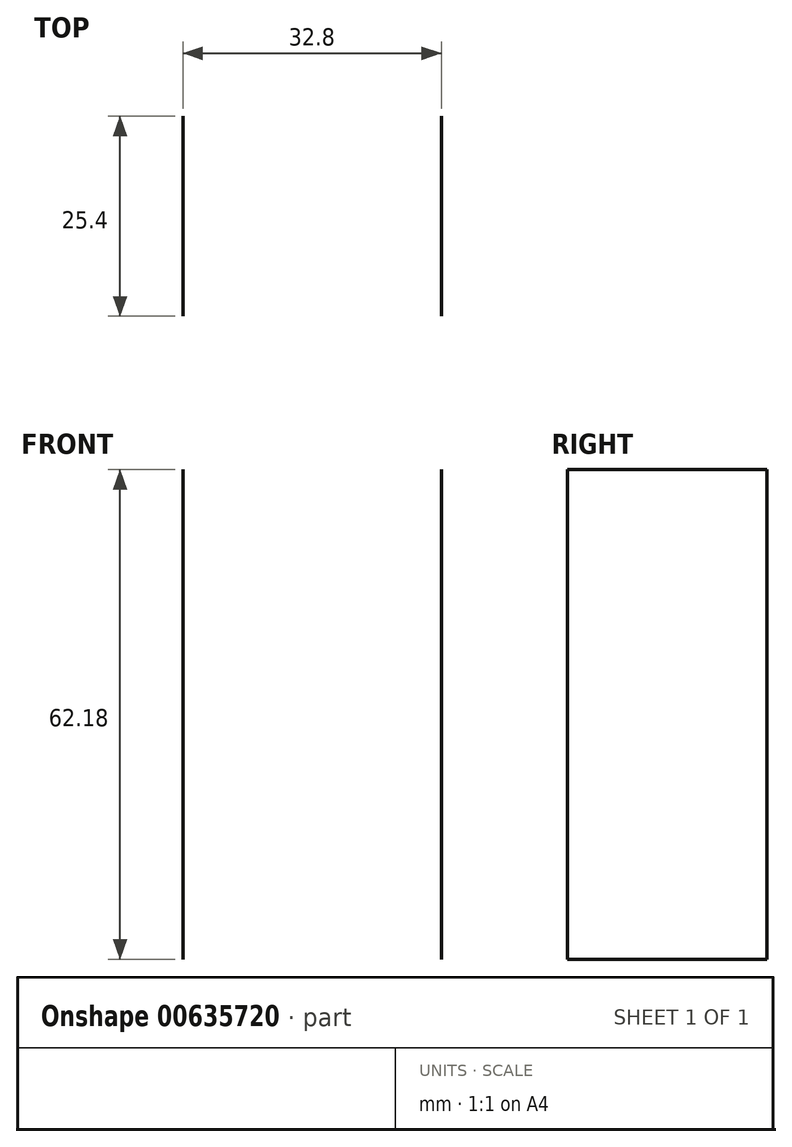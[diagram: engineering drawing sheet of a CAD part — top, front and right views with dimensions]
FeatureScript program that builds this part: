
annotation { "Feature Type Name" : "Feature", "Feature Type Description" : "" }
export const myFeature = defineFeature(function(context is Context, id is Id, definition is map)
    precondition{}
    {
        {
            var Q0;
            Q0=qCreatedBy(makeId("Front.planeOp"),FACE);
            var sketch = newSketch(context, id + "F0", { "sketchPlane" : qUnion([Q0])});
            skSolve(sketch);
        }
        {
            var Q0;
            Q0=qCreatedBy(makeId("Front.planeOp"),FACE);
            var sketch = newSketch(context, id + "F1", { "sketchPlane" : qUnion([Q0])});
            skLineSegment(sketch, "E0.bottom", {"start": v(-48.35, 50.77) * mm, "end": v(-15.55, 50.77) * mm});
            skLineSegment(sketch, "E0.top", {"start": v(-48.35, -11.4) * mm, "end": v(-15.55, -11.4) * mm});
            skLineSegment(sketch, "E0.left", {"start": v(-48.35, 50.77) * mm, "end": v(-48.35, -11.4) * mm});
            skLineSegment(sketch, "E0.right", {"start": v(-15.55, 50.77) * mm, "end": v(-15.55, -11.4) * mm});
            skSolve(sketch);
        }
        {
            var Q0;
            Q0=sQuery(id+"F1.wireOp",EDGE,"E0.left");
            var Q1;
            Q1=sQuery(id+"F1.wireOp",EDGE,"E0.right");
            var Q2;
            Q2 = qConstructionFilter(qBodyType(qCreatedBy(id + "F0" ,EDGE), BodyType.WIRE), ConstructionObject.NO);
            extrude(context, id + "F2", {"bodyType" : ToolBodyType.SURFACE, "surfaceEntities" : qUnion([Q0, Q1, Q2]), "depth" : 25.4 * mm, "offsetDistance" : 25.4 * mm});
        }
    });
